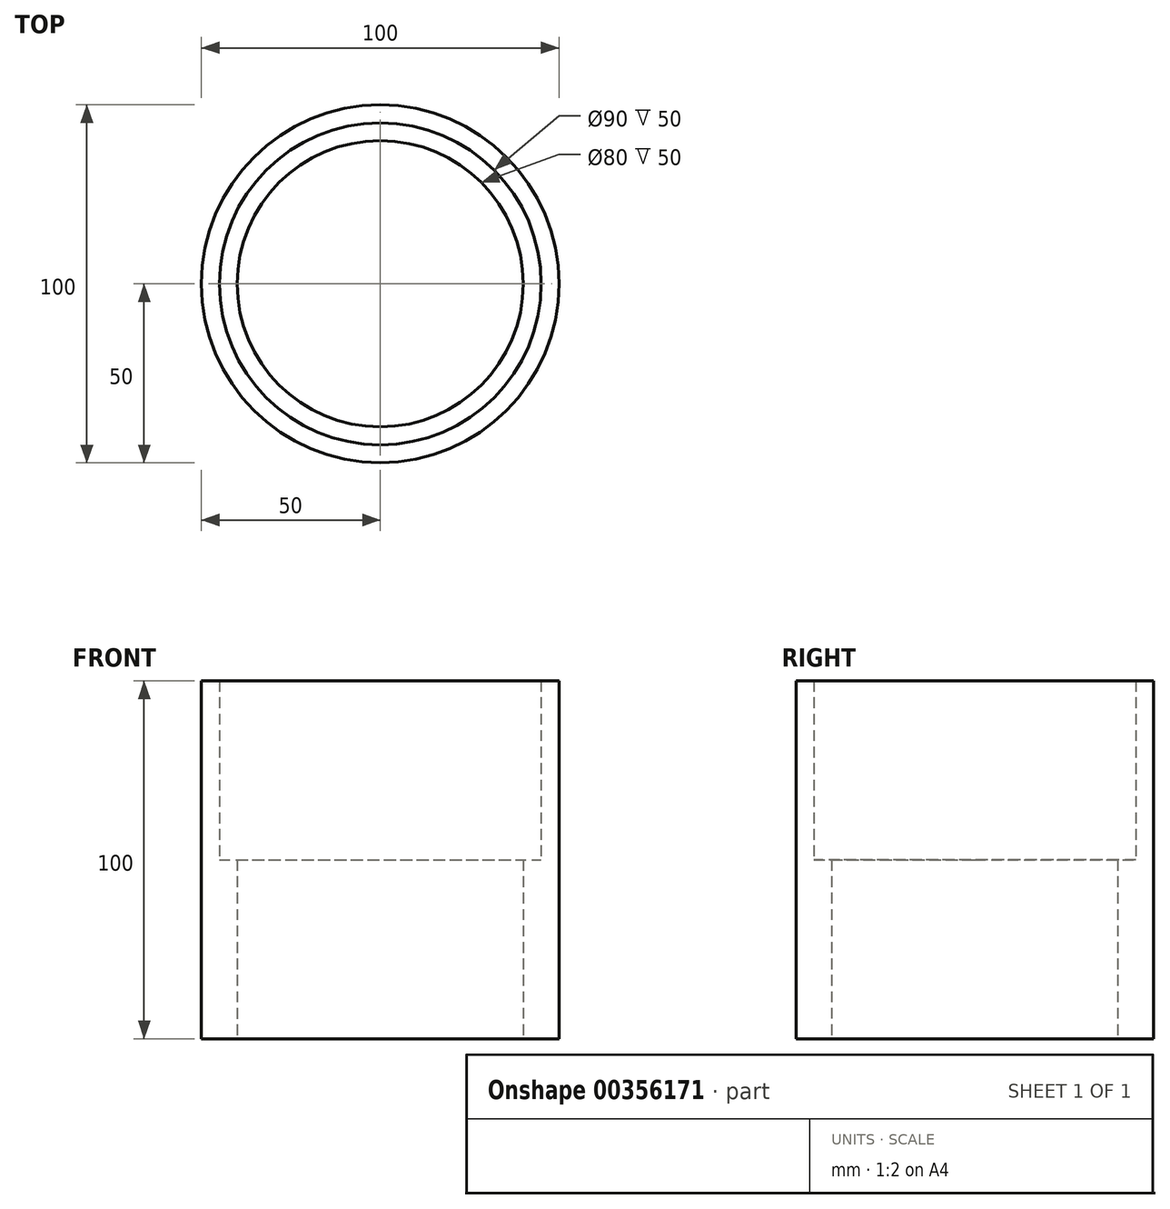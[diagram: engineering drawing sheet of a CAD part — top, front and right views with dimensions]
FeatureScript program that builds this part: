
annotation { "Feature Type Name" : "Feature", "Feature Type Description" : "" }
export const myFeature = defineFeature(function(context is Context, id is Id, definition is map)
    precondition{}
    {
        {
            var Q0;
            Q0=qCreatedBy(makeId("Front.planeOp"),FACE);
            var sketch = newSketch(context, id + "F0", { "sketchPlane" : qUnion([Q0])});
            skLineSegment(sketch, "E0.bottom", {"start": v(0, 0) * mm, "end": v(-5, 0) * mm});
            skLineSegment(sketch, "E0.top", {"start": v(0, 50) * mm, "end": v(-5, 50) * mm});
            skLineSegment(sketch, "E0.left", {"start": v(0, 0) * mm, "end": v(0, 50) * mm});
            skLineSegment(sketch, "E0.right", {"start": v(-5, 0) * mm, "end": v(-5, 50) * mm});
            skLineSegment(sketch, "E1.bottom", {"start": v(-5, 0) * mm, "end": v(-10, 0) * mm});
            skLineSegment(sketch, "E1.top", {"start": v(-5, 100) * mm, "end": v(-10, 100) * mm});
            skLineSegment(sketch, "E1.left", {"start": v(-5, 0) * mm, "end": v(-5, 100) * mm});
            skLineSegment(sketch, "E1.right", {"start": v(-10, 0) * mm, "end": v(-10, 100) * mm});
            skLineSegment(sketch, "E2.bottom", {"start": v(0, 0) * mm, "end": v(40, 0) * mm});
            skLineSegment(sketch, "E2.top", {"start": v(0, 5) * mm, "end": v(40, 5) * mm});
            skLineSegment(sketch, "E2.left", {"start": v(0, 0) * mm, "end": v(0, 5) * mm});
            skLineSegment(sketch, "E2.right", {"start": v(40, 0) * mm, "end": v(40, 5) * mm});
            skSolve(sketch);
        }
        {
            var Q0;
            {var subQ2=sQuery(id+"F0.wireOp",EDGE,"E0.bottom");Q0=makeQuery(id+"F0.imprint","IMPRINT",FACE,{"disambiguationData":[TD([[makeQuery(id+"F0.imprint","IMPRINT",EDGE,{"derivedFrom":subQ2}),-1.0]])]});}
            var Q1;
            {var subQ3=sQuery(id+"F0.wireOp",EDGE,"E1.bottom");Q1=makeQuery(id+"F0.imprint","IMPRINT",FACE,{"disambiguationData":[TD([[makeQuery(id+"F0.imprint","IMPRINT",EDGE,{"derivedFrom":subQ3}),-1.0]])]});}
            var Q2;
            Q2=sQuery(id+"F0.wireOp",EDGE,"E2.right");
            revolve(context, id + "F1", {"entities" : qUnion([Q0, Q1]), "axis" : qUnion([Q2]), "revolveType" : RevolveType.FULL});
        }
    });
